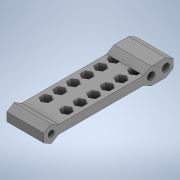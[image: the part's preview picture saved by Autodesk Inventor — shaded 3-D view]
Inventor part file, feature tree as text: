
AUTODESK INVENTOR PART (.ipt)
format: ipt  version: 2020 (Build 240168000, 168)  size: 401,920 bytes
history: native  units: in
note: dims shown in document units (in); Inventor stores cm internally (conversion verified against a paired STEP export)
features: sketch x6, extrude x5, projected_geometry x3, plane x1, mirror x1
ambient origin geometry x8: Origin, YZ Plane, XZ Plane, XY Plane, X Axis, Y Axis, Z Axis, Center Point
bodies: Solid1 (feature_tree)
feature tree (16):
  extrude  "Extrusion1"  Depth=2.7559in
  plane  "Work Plane1"
  extrude  "Extrusion2"  Depth=0.7874in
  extrude  "Extrusion3"  Depth=0.0787in
  sketch  "Sketch4"  dims[d6=0.7874in d7=0.0in d8=0.0787in]
  extrude  "Extrusion4"  Depth=0.0787in
  extrude  "Extrusion5"  Depth=0.0787in
  mirror  "Mirror1"
  sketch  "Sketch1"  dims[d0=0.1818in d1=2.7559in]
  sketch  "Sketch2"  dims[d2=0.1299in d3=0.7874in]
  sketch  "Sketch3"  dims[d4=0.0in d5=0.0787in]
  projected_geometry  "Projected Loop1"
  sketch  "Sketch5"  dims[d9=0.0787in d10=0.0787in]
  sketch  "Sketch6"  dims[d11=0.2273in d12=3.937in d14=0.2903in d15=0.3937in d17=0.3937in d19=3.937in d21=0.2903in d22=0.3937in d24=0.3937in d26=0.7874in d27=0.0in d28=2.4409in d29=0.315in d31=0.315in d33=0.1575in d34=0.2362in d35=0.0in d36=0.2756in d37=-0.3092in d38=0.315in]
  projected_geometry  "Projected Loop2"
  projected_geometry  "Projected Loop3"
